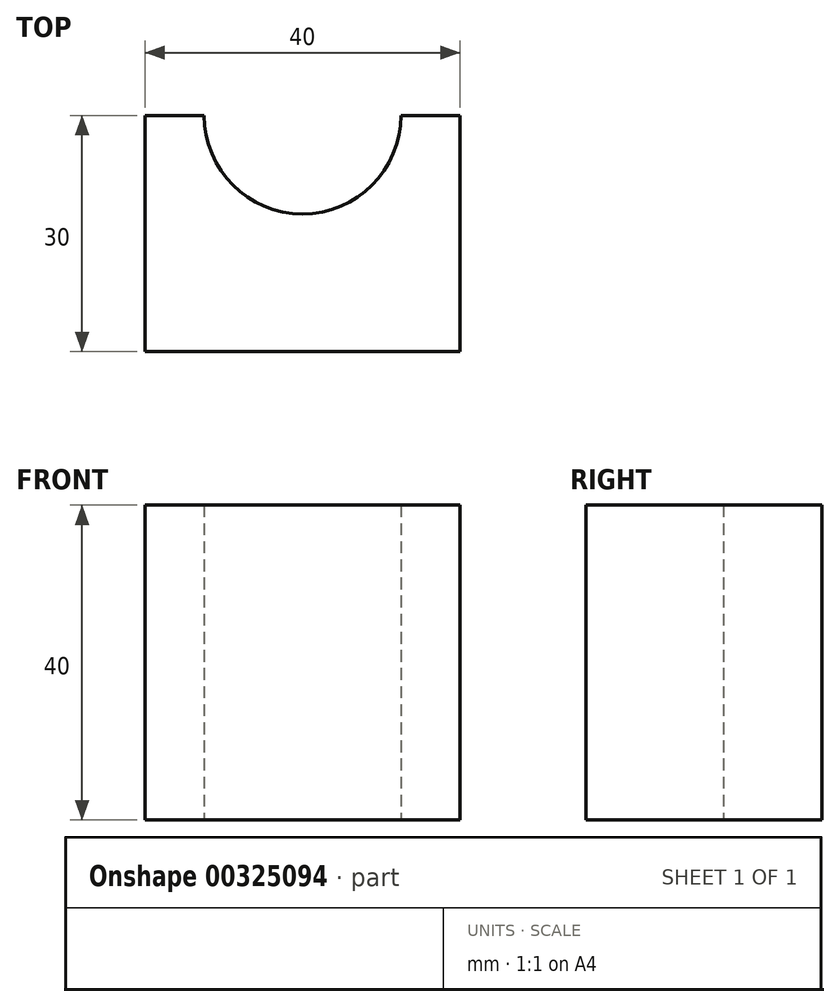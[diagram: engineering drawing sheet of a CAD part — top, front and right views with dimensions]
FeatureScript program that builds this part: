
annotation { "Feature Type Name" : "Feature", "Feature Type Description" : "" }
export const myFeature = defineFeature(function(context is Context, id is Id, definition is map)
    precondition{}
    {
        {
            var Q0;
            Q0=qCreatedBy(makeId("Top.planeOp"),FACE);
            var sketch = newSketch(context, id + "F0", { "sketchPlane" : qUnion([Q0])});
            skLineSegment(sketch, "E0.bottom", {"start": v(20, -15) * mm, "end": v(-20, -15) * mm});
            skLineSegment(sketch, "E0.top", {"start": v(20, 15) * mm, "end": v(12.5, 15) * mm});
            skLineSegment(sketch, "E0.left", {"start": v(20, -15) * mm, "end": v(20, 15) * mm});
            skLineSegment(sketch, "E0.right", {"start": v(-20, -15) * mm, "end": v(-20, 15) * mm});
            skPoint(sketch, "E0.middle", {"position": v(0, 0) * mm});
            skPoint(sketch, "E1", {"position": v(0, 2.5) * mm});
            skLineSegment(sketch, "E2", {"start": v(-12.5, 15) * mm, "end": v(-20, 15) * mm});
            skArc(sketch, "E3", {"start": v(-12.5, 15) * mm, "mid": v(0, 2.5) * mm, "end": v(12.5, 15) * mm});
            skSolve(sketch);
        }
        {
            var Q0;
            Q0=makeQuery(id+"F0.imprint","IMPRINT",FACE,{"disambiguationData":[TD([[makeQuery(id+"F0.imprint","IMPRINT",EDGE,{"derivedFrom":sQuery(id+"F0.wireOp",EDGE,"E0.bottom")}),-1.0]])]});
            extrude(context, id + "F1", {"entities" : qUnion([Q0]), "depth" : 40 * mm});
        }
    });
